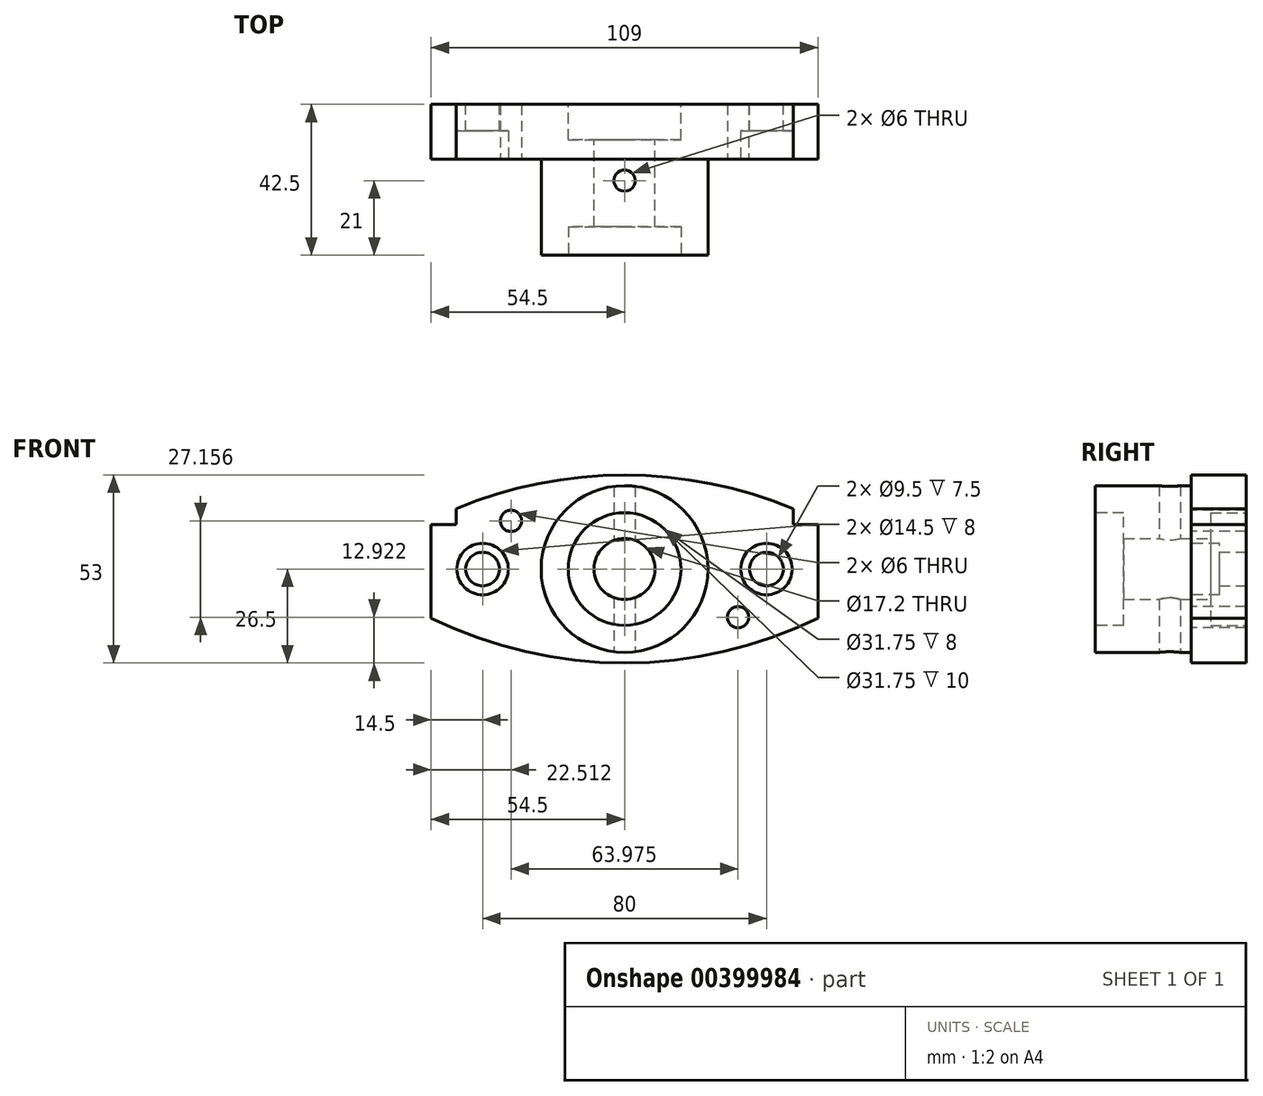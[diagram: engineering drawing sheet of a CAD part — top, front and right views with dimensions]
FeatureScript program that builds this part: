
annotation { "Feature Type Name" : "Feature", "Feature Type Description" : "" }
export const myFeature = defineFeature(function(context is Context, id is Id, definition is map)
    precondition{}
    {
        {
            var Q0;
            Q0=qCreatedBy(makeId("Front.planeOp"),FACE);
            var sketch = newSketch(context, id + "F0", { "sketchPlane" : qUnion([Q0])});
            skLineSegment(sketch, "E0.bottom", {"start": v(54.5, -26.5) * mm, "end": v(-54.5, -26.5) * mm});
            skLineSegment(sketch, "E0.top", {"start": v(54.5, 26.5) * mm, "end": v(-54.5, 26.5) * mm, "construction": true});
            skLineSegment(sketch, "E0.left", {"start": v(54.5, -26.5) * mm, "end": v(54.5, 26.5) * mm});
            skLineSegment(sketch, "E0.right", {"start": v(-54.5, -26.5) * mm, "end": v(-54.5, 26.5) * mm});
            skPoint(sketch, "E0.middle", {"position": v(0, 0) * mm});
            skArc(sketch, "E1", {"start": v(47.5, 17) * mm, "mid": v(0, 26.5) * mm, "end": v(-47.5, 17) * mm});
            skArc(sketch, "E2", {"start": v(-54.5, -13.82) * mm, "mid": v(0, -26.5) * mm, "end": v(54.5, -13.82) * mm});
            skLineSegment(sketch, "E3", {"start": v(47.5, 17) * mm, "end": v(47.5, 12.5) * mm});
            skLineSegment(sketch, "E4", {"start": v(47.5, 12.5) * mm, "end": v(54.5, 12.5) * mm});
            skLineSegment(sketch, "E5", {"start": v(-47.5, 12.5) * mm, "end": v(-47.5, 17) * mm});
            skPoint(sketch, "E6.orphan", {"position": v(54.5, 13.82) * mm});
            skPoint(sketch, "E7.orphan", {"position": v(-54.5, 13.82) * mm});
            skLineSegment(sketch, "E8", {"start": v(-47.5, 12.5) * mm, "end": v(-54.5, 12.5) * mm});
            skLineSegment(sketch, "E9", {"start": v(47.5, 12.5) * mm, "end": v(47.5, -17) * mm, "construction": true});
            skCircle(sketch, "E10", {"center": v(0, 0) * mm, "radius": 8.6 * mm});
            skCircle(sketch, "E11", {"center": v(-40, 0) * mm, "radius": 4.75 * mm});
            skCircle(sketch, "E12", {"center": v(40, 0) * mm, "radius": 4.75 * mm});
            skLineSegment(sketch, "E13", {"start": v(0, 0) * mm, "end": v(0, 26.5) * mm, "construction": true});
            skPoint(sketch, "E13.endSnap0", {"position": v(0, 26.5) * mm});
            skSolve(sketch);
        }
        {
            var Q0;
            Q0=makeQuery(id+"F0.imprint","IMPRINT",FACE,{"disambiguationData":[TD([[makeQuery(id+"F0.imprint","IMPRINT",EDGE,{"derivedFrom":sQuery(id+"F0.wireOp",EDGE,"E1")}),1.0]])]});
            var Q1;
            Q1=makeQuery(id+"F0.imprint","IMPRINT",FACE,{"disambiguationData":[TD([[makeQuery(id+"F0.imprint","IMPRINT",EDGE,{"derivedFrom":sQuery(id+"F0.wireOp",EDGE,"E10")}),-1.0]])]});
            extrude(context, id + "F1", {"entities" : qUnion([Q0, Q1]), "depth" : 15.5 * mm});
        }
        {
            var Q0;
            Q0=makeQuery(id+"F1.opExtrude","CAP_FACE",FACE,{"disambiguationData":[OSD([sQuery(id+"F0.wireOp",EDGE,"E0.left"),sQuery(id+"F0.wireOp",EDGE,"E0.right"),sQuery(id+"F0.wireOp",EDGE,"E1"),sQuery(id+"F0.wireOp",EDGE,"E2"),sQuery(id+"F0.wireOp",EDGE,"E3"),sQuery(id+"F0.wireOp",EDGE,"E4"),sQuery(id+"F0.wireOp",EDGE,"E5"),sQuery(id+"F0.wireOp",EDGE,"E8"),sQuery(id+"F0.wireOp",EDGE,"E10"),sQuery(id+"F0.wireOp",EDGE,"E11"),sQuery(id+"F0.wireOp",EDGE,"E12")])],"isStart":false});
            var sketch = newSketch(context, id + "F2", { "sketchPlane" : qUnion([Q0])});
            skCircle(sketch, "E14", {"center": v(-40, 0) * mm, "radius": 7.25 * mm});
            skCircle(sketch, "E15", {"center": v(40, 0) * mm, "radius": 7.25 * mm});
            skSolve(sketch);
        }
        {
            var Q0;
            Q0=qSketchRegion(id+"F2",true);
            extrude(context, id + "F3", {"entities" : qUnion([Q0]), "operationType" : NewBodyOperationType.REMOVE, "oppositeDirection" : true, "depth" : 8 * mm});
        }
        {
            var Q0;
            Q0=makeQuery(id+"F1.opExtrude","CAP_FACE",FACE,{"disambiguationData":[OSD([sQuery(id+"F0.wireOp",EDGE,"E0.left"),sQuery(id+"F0.wireOp",EDGE,"E0.right"),sQuery(id+"F0.wireOp",EDGE,"E1"),sQuery(id+"F0.wireOp",EDGE,"E2"),sQuery(id+"F0.wireOp",EDGE,"E3"),sQuery(id+"F0.wireOp",EDGE,"E4"),sQuery(id+"F0.wireOp",EDGE,"E5"),sQuery(id+"F0.wireOp",EDGE,"E8"),sQuery(id+"F0.wireOp",EDGE,"E10"),sQuery(id+"F0.wireOp",EDGE,"E11"),sQuery(id+"F0.wireOp",EDGE,"E12")])],"isStart":false});
            var sketch = newSketch(context, id + "F4", { "sketchPlane" : qUnion([Q0])});
            skCircle(sketch, "E16", {"center": v(0, 0) * mm, "radius": 23.5 * mm});
            skCircle(sketch, "E17", {"center": v(0, 0) * mm, "radius": 8.6 * mm});
            skSolve(sketch);
        }
        {
            var Q0;
            Q0=qSketchRegion(id+"F4",true);
            extrude(context, id + "F5", {"entities" : qUnion([Q0]), "operationType" : NewBodyOperationType.ADD, "depth" : (42.5 - 15.5) * mm});
        }
        {
            var Q0;
            Q0=makeQuery(id+"F5.opExtrude","CAP_FACE",FACE,{"disambiguationData":[OSD([sQuery(id+"F4.wireOp",EDGE,"E16"),sQuery(id+"F4.wireOp",EDGE,"E17")])],"isStart":false});
            var sketch = newSketch(context, id + "F6", { "sketchPlane" : qUnion([Q0])});
            skCircle(sketch, "E18", {"center": v(0, 0) * mm, "radius": 15.88 * mm});
            skSolve(sketch);
        }
        {
            var Q0;
            Q0=qSketchRegion(id+"F6",true);
            extrude(context, id + "F7", {"entities" : qUnion([Q0]), "operationType" : NewBodyOperationType.REMOVE, "oppositeDirection" : true, "depth" : 8 * mm});
        }
        {
            var Q0;
            Q0=makeQuery(id+"F1.opExtrude","CAP_FACE",FACE,{"disambiguationData":[OSD([sQuery(id+"F0.wireOp",EDGE,"E0.left"),sQuery(id+"F0.wireOp",EDGE,"E0.right"),sQuery(id+"F0.wireOp",EDGE,"E1"),sQuery(id+"F0.wireOp",EDGE,"E2"),sQuery(id+"F0.wireOp",EDGE,"E3"),sQuery(id+"F0.wireOp",EDGE,"E4"),sQuery(id+"F0.wireOp",EDGE,"E5"),sQuery(id+"F0.wireOp",EDGE,"E8"),sQuery(id+"F0.wireOp",EDGE,"E10"),sQuery(id+"F0.wireOp",EDGE,"E11"),sQuery(id+"F0.wireOp",EDGE,"E12")])],"isStart":true});
            var sketch = newSketch(context, id + "F8", { "sketchPlane" : qUnion([Q0])});
            skCircle(sketch, "E19", {"center": v(0, 0) * mm, "radius": 15.88 * mm});
            skSolve(sketch);
        }
        {
            var Q0;
            Q0=qSketchRegion(id+"F8",true);
            extrude(context, id + "F9", {"entities" : qUnion([Q0]), "operationType" : NewBodyOperationType.REMOVE, "oppositeDirection" : true, "depth" : 10 * mm});
        }
        {
            var Q0;
            Q0=makeQuery(id+"F1.opExtrude","CAP_EDGE",EDGE,{"disambiguationData":[OSD([sQuery(id+"F0.wireOp",EDGE,"E0.right")])],"isStart":false});
            cPoint(context, id + "F10", {"entities" : qUnion([Q0]), "parameter" : 0.5});
        }
        {
            var Q0;
            Q0=makeQuery(id+"F1.opExtrude","CAP_EDGE",EDGE,{"disambiguationData":[OSD([sQuery(id+"F0.wireOp",EDGE,"E0.right")])],"isStart":true});
            cPoint(context, id + "F11", {"entities" : qUnion([Q0]), "parameter" : 0.5});
        }
        {
            var Q0;
            Q0=makeQuery(id+"F1.opExtrude","CAP_EDGE",EDGE,{"disambiguationData":[OSD([sQuery(id+"F0.wireOp",EDGE,"E0.left")])],"isStart":false});
            cPoint(context, id + "F12", {"entities" : qUnion([Q0]), "parameter" : 0.5});
        }
        {
            var Q0;
            Q0=qCreatedBy(id+"F10",VERTEX);
            var Q1;
            Q1=qCreatedBy(id+"F11",VERTEX);
            var Q2;
            Q2=qCreatedBy(id+"F12",VERTEX);
            cPlane(context, id + "F13", {"entities" : qUnion([Q0, Q1, Q2]), "cplaneType" : CPlaneType.THREE_POINT, "offset" : 25 * mm, "width" : 150 * mm, "height" : 150 * mm});
        }
        {
            var Q0;
            Q0=qCreatedBy(id+"F13.planeOp",FACE);
            var sketch = newSketch(context, id + "F14", { "sketchPlane" : qUnion([Q0])});
            skCircle(sketch, "E20", {"center": v(0, -21.5) * mm, "radius": 3 * mm});
            skSolve(sketch);
        }
        {
            var Q0;
            Q0=makeQuery(id+"F14.imprint","IMPRINT",FACE,{"disambiguationData":[TD([[makeQuery(id+"F14.imprint","IMPRINT",EDGE,{"derivedFrom":sQuery(id+"F14.wireOp",EDGE,"E20")}),1.0]])]});
            extrude(context, id + "F15", {"entities" : qUnion([Q0]), "operationType" : NewBodyOperationType.REMOVE, "depth" : 25 * mm, "hasSecondDirection" : true, "secondDirectionOppositeDirection" : true, "secondDirectionDepth" : 25 * mm});
        }
        {
            var Q0;
            Q0=makeQuery(id+"F1.opExtrude","CAP_FACE",FACE,{"disambiguationData":[OSD([sQuery(id+"F0.wireOp",EDGE,"E0.left"),sQuery(id+"F0.wireOp",EDGE,"E0.right"),sQuery(id+"F0.wireOp",EDGE,"E1"),sQuery(id+"F0.wireOp",EDGE,"E2"),sQuery(id+"F0.wireOp",EDGE,"E3"),sQuery(id+"F0.wireOp",EDGE,"E4"),sQuery(id+"F0.wireOp",EDGE,"E5"),sQuery(id+"F0.wireOp",EDGE,"E8"),sQuery(id+"F0.wireOp",EDGE,"E10"),sQuery(id+"F0.wireOp",EDGE,"E11"),sQuery(id+"F0.wireOp",EDGE,"E12")])],"isStart":false});
            var sketch = newSketch(context, id + "F16", { "sketchPlane" : qUnion([Q0])});
            skCircle(sketch, "E21", {"center": v(-31.99, 13.58) * mm, "radius": 3 * mm});
            skCircle(sketch, "E22", {"center": v(31.99, -13.58) * mm, "radius": 3 * mm});
            skLineSegment(sketch, "E23", {"start": v(-31.99, 13.58) * mm, "end": v(31.99, -13.58) * mm, "construction": true});
            skCircle(sketch, "E24", {"center": v(0, 0) * mm, "radius": 3 * mm, "construction": true});
            skLineSegment(sketch, "E25", {"start": v(0, 0) * mm, "end": v(-31.99, 0) * mm, "construction": true});
            skSolve(sketch);
        }
        {
            var Q0;
            Q0=qSketchRegion(id+"F16",true);
            extrude(context, id + "F17", {"entities" : qUnion([Q0]), "operationType" : NewBodyOperationType.REMOVE, "endBound" : BoundingType.UP_TO_NEXT, "oppositeDirection" : true, "depth" : 25 * mm});
        }
    });
